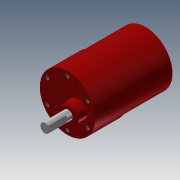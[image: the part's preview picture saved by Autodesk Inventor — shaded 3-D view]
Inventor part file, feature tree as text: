
AUTODESK INVENTOR PART (.ipt)
format: ipt  version: 2015 (Build 190159000, 159)  size: 154,624 bytes
history: native  units: mm
features: sketch x9, extrude x6, fillet x1, chamfer x1, hole x1
ambient origin geometry x8: Origin, YZ Plane, XZ Plane, XY Plane, X Axis, Y Axis, Z Axis, Center Point
bodies: Solid1 (feature_tree)
feature tree (18):
  extrude  "Extrusion1"  Depth=22.0mm TaperAngle=0.0deg
  extrude  "Extrusion2"  Depth=0.5mm TaperAngle=0.0deg
  fillet  "Fillet1"  Radius=0.5mm
  extrude  "Extrusion3"  Depth=12.0mm
  extrude  "Extrusion4"  Depth=6.0mm
  extrude  "Extrusion5"  Depth=12.0mm TaperAngle=0.0deg
  chamfer  "Chamfer1"  Distance=1.0mm Angle=45.0deg
  extrude  "Extrusion6"  Depth=12.0mm TaperAngle=0.0deg
  hole  "Hole1"  [1 undecoded]
  sketch  "Sketch8"  dims[d24=2.4mm]
  sketch  "Sketch9"  dims[d28=2.4mm d29=2.4mm d32=2.4mm d33=15.5mm d34=2.4mm d35=2.459mm d36=3.0mm d37=4.0mm d38=2.0mm d39=90.0deg d40=3.0mm d41=0.0mm]
  sketch  "Sketch1"  dims[d0=36.8mm d1=22.0mm d2=0.0mm]
  sketch  "Sketch2"  dims[d3=35.8mm d4=30.0mm d5=0.0mm d6=0.5mm]
  sketch  "Sketch3"  dims[d7=7.0mm d8=12.0mm]
  sketch  "Sketch4"  dims[d9=6.5mm d10=0.0mm d11=6.0mm]
  sketch  "Sketch5"  dims[d12=3.5mm d13=0.0mm d14=12.0mm d15=0.0mm d16=1.0mm d17=2.0mm d18=45.0deg]
  sketch  "Sketch6"  dims[d19=0.6mm d20=12.0mm d21=0.0mm]
  sketch  "Sketch7"  dims[d22=31.0mm d23=2.4mm]
note: 1 required parameter value undecoded (feature->parameter linkage not recoverable at this tier; creation-order binding heuristic only, values carry confidence <= 0.55)
